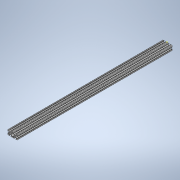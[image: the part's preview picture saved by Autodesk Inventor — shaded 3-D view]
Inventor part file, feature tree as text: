
AUTODESK INVENTOR PART (.ipt)
format: ipt  version: 2020 (Build 240168000, 168)  size: 338,432 bytes
history: native  units: in
note: dims shown in document units (in); Inventor stores cm internally (conversion verified against a paired STEP export)
features: sketch x2, extrude x1
ambient origin geometry x8: Origin, YZ Plane, XZ Plane, XY Plane, X Axis, Y Axis, Z Axis, Center Point
bodies: Solid1 (feature_tree)
feature tree (3):
  extrude  "Extrusion1"  [1 undecoded]
  sketch  "Sketch2"
  sketch  "Sketch1"  dims[d0=32.0in d1=0.0in]
note: 1 required parameter value undecoded (feature->parameter linkage not recoverable at this tier; creation-order binding heuristic only, values carry confidence <= 0.55)
